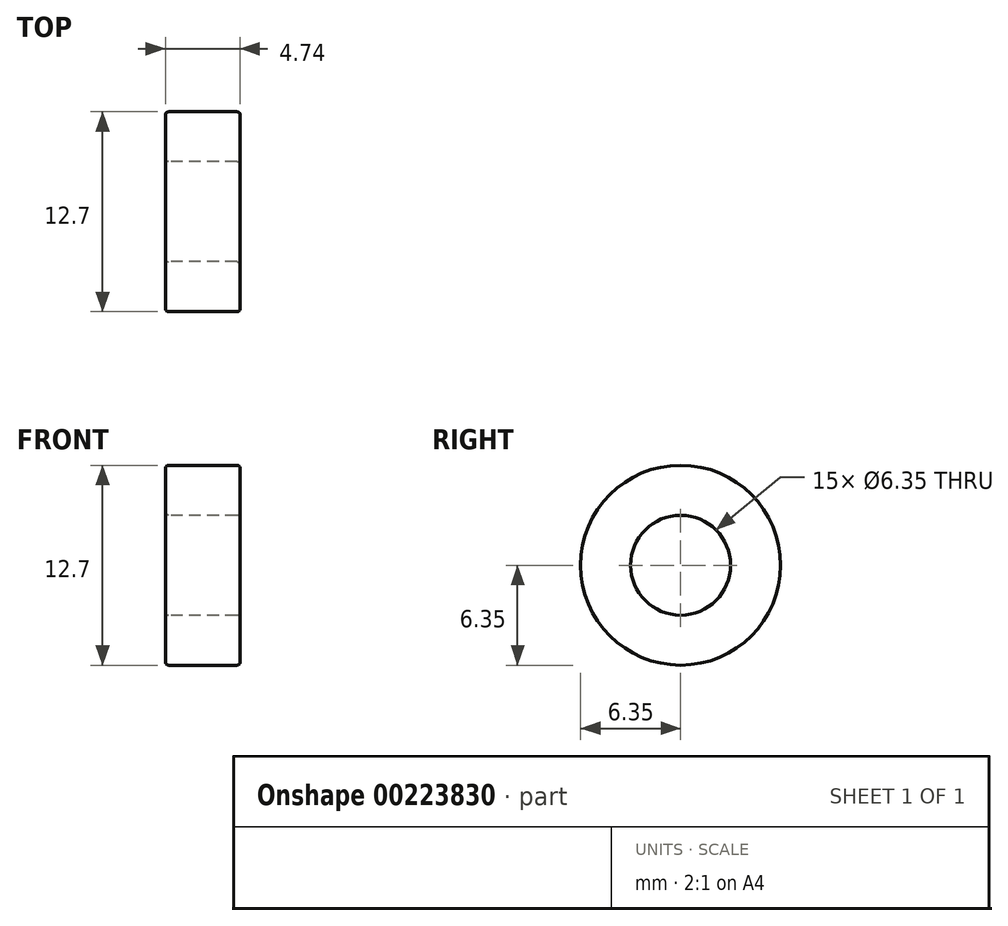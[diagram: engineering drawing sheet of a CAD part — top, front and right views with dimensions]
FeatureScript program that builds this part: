
annotation { "Feature Type Name" : "Feature", "Feature Type Description" : "" }
export const myFeature = defineFeature(function(context is Context, id is Id, definition is map)
    precondition{}
    {
        {
            var Q0;
            Q0=qCreatedBy(makeId("Right.planeOp"),FACE);
            var sketch = newSketch(context, id + "F0", { "sketchPlane" : qUnion([Q0])});
            skCircle(sketch, "E0", {"center": v(0, 0) * mm, "radius": 3.18 * mm});
            skCircle(sketch, "E1", {"center": v(0, 0) * mm, "radius": 6.35 * mm});
            skSolve(sketch);
        }
        {
            var Q0;
            Q0=makeQuery(id+"F0.imprint","IMPRINT",FACE,{"disambiguationData":[TD([[makeQuery(id+"F0.imprint","IMPRINT",EDGE,{"derivedFrom":sQuery(id+"F0.wireOp",EDGE,"E0")}),-1.0]])]});
            var Q1;
            Q1=sQuery(id+"F0.wireOp",EDGE,"E0");
            var Q2;
            Q2=sQuery(id+"F0.wireOp",EDGE,"E1");
            extrude(context, id + "F1", {"entities" : qUnion([Q0]), "surfaceEntities" : qUnion([Q1, Q2]), "endBound" : BoundingType.SYMMETRIC, "depth" : 4.75 * mm});
        }
        {
            var Q0;
            Q0=makeQuery(id+"F1.opExtrude","CAP_EDGE",EDGE,{"disambiguationData":[OSD([sQuery(id+"F0.wireOp",EDGE,"E1")])],"isStart":false});
            fillet(context, id + "F2", {"entities" : qUnion([Q0]), "radius" : 0.2 * mm, "tangentPropagation" : true, "allowEdgeOverflow" : false});
        }
        {
            var Q0;
            Q0=makeQuery(id+"F1.opExtrude","CAP_EDGE",EDGE,{"disambiguationData":[OSD([sQuery(id+"F0.wireOp",EDGE,"E0")])],"isStart":false});
            fillet(context, id + "F3", {"entities" : qUnion([Q0]), "radius" : 0.2 * mm, "tangentPropagation" : true, "allowEdgeOverflow" : false});
        }
        {
            var Q0;
            Q0=makeQuery(id+"F1.opExtrude","CAP_EDGE",EDGE,{"disambiguationData":[OSD([sQuery(id+"F0.wireOp",EDGE,"E1")])],"isStart":true});
            fillet(context, id + "F4", {"entities" : qUnion([Q0]), "radius" : 0.2 * mm, "tangentPropagation" : true, "allowEdgeOverflow" : false});
        }
        {
            var Q0;
            Q0=makeQuery(id+"F1.opExtrude","CAP_EDGE",EDGE,{"disambiguationData":[OSD([sQuery(id+"F0.wireOp",EDGE,"E0")])],"isStart":true});
            fillet(context, id + "F5", {"entities" : qUnion([Q0]), "radius" : 0.2 * mm, "tangentPropagation" : true, "allowEdgeOverflow" : false});
        }
    });
